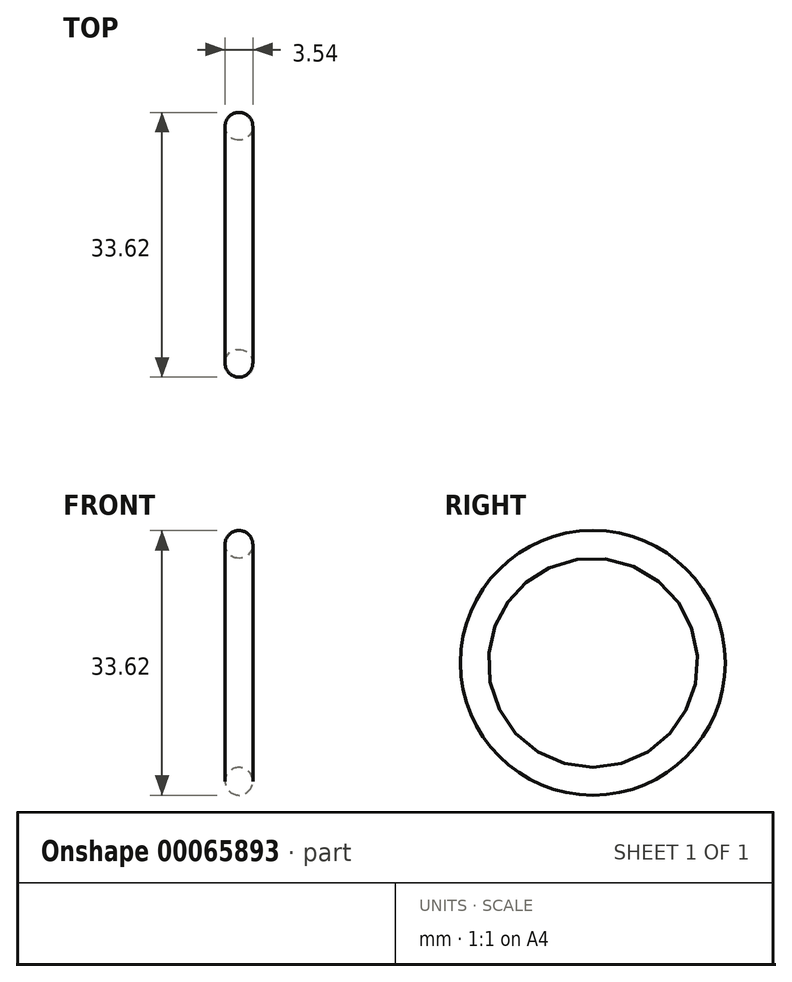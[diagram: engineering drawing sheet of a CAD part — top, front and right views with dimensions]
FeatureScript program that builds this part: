
annotation { "Feature Type Name" : "Feature", "Feature Type Description" : "" }
export const myFeature = defineFeature(function(context is Context, id is Id, definition is map)
    precondition{}
    {
        {
            var Q0;
            Q0=qCreatedBy(makeId("Front.planeOp"),FACE);
            var sketch = newSketch(context, id + "F0", { "sketchPlane" : qUnion([Q0])});
            skLineSegment(sketch, "E0", {"start": v(0, 0) * mm, "end": v(-6.06, 0) * mm, "construction": true});
            skCircle(sketch, "E1", {"center": v(0, 15.05) * mm, "radius": 1.77 * mm});
            skSolve(sketch);
        }
        {
            var Q0;
            Q0=makeQuery(id+"F0.imprint","IMPRINT",FACE,{"disambiguationData":[TD([[makeQuery(id+"F0.imprint","IMPRINT",EDGE,{"derivedFrom":sQuery(id+"F0.wireOp",EDGE,"E1")}),1.0]])]});
            var Q1;
            Q1=sQuery(id+"F0.wireOp",EDGE,"E0");
            revolve(context, id + "F1", {"entities" : qUnion([Q0]), "axis" : qUnion([Q1]), "revolveType" : RevolveType.FULL});
        }
    });
